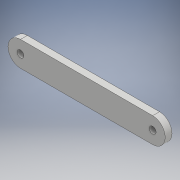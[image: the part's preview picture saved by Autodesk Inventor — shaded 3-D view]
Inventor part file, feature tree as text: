
AUTODESK INVENTOR PART (.ipt)
format: ipt  version: 2018 (Build 220112000, 112)  size: 105,472 bytes
history: native  units: mm
features: other x1, extrude x1, sketch x1
ambient origin geometry x8: Origin, YZ Plane, XZ Plane, XY Plane, X Axis, Y Axis, Z Axis, Center Point
bodies: Body1 (feature_tree)
feature tree (3):
  other  "Sólido1"
  extrude  "Extrusión1"  Depth=3.0mm
  sketch  "Boceto1"  dims[d26=30.0mm d125=16.0mm d172=3.0mm d173=3.0mm d174=3.0mm d175=0.0mm]
